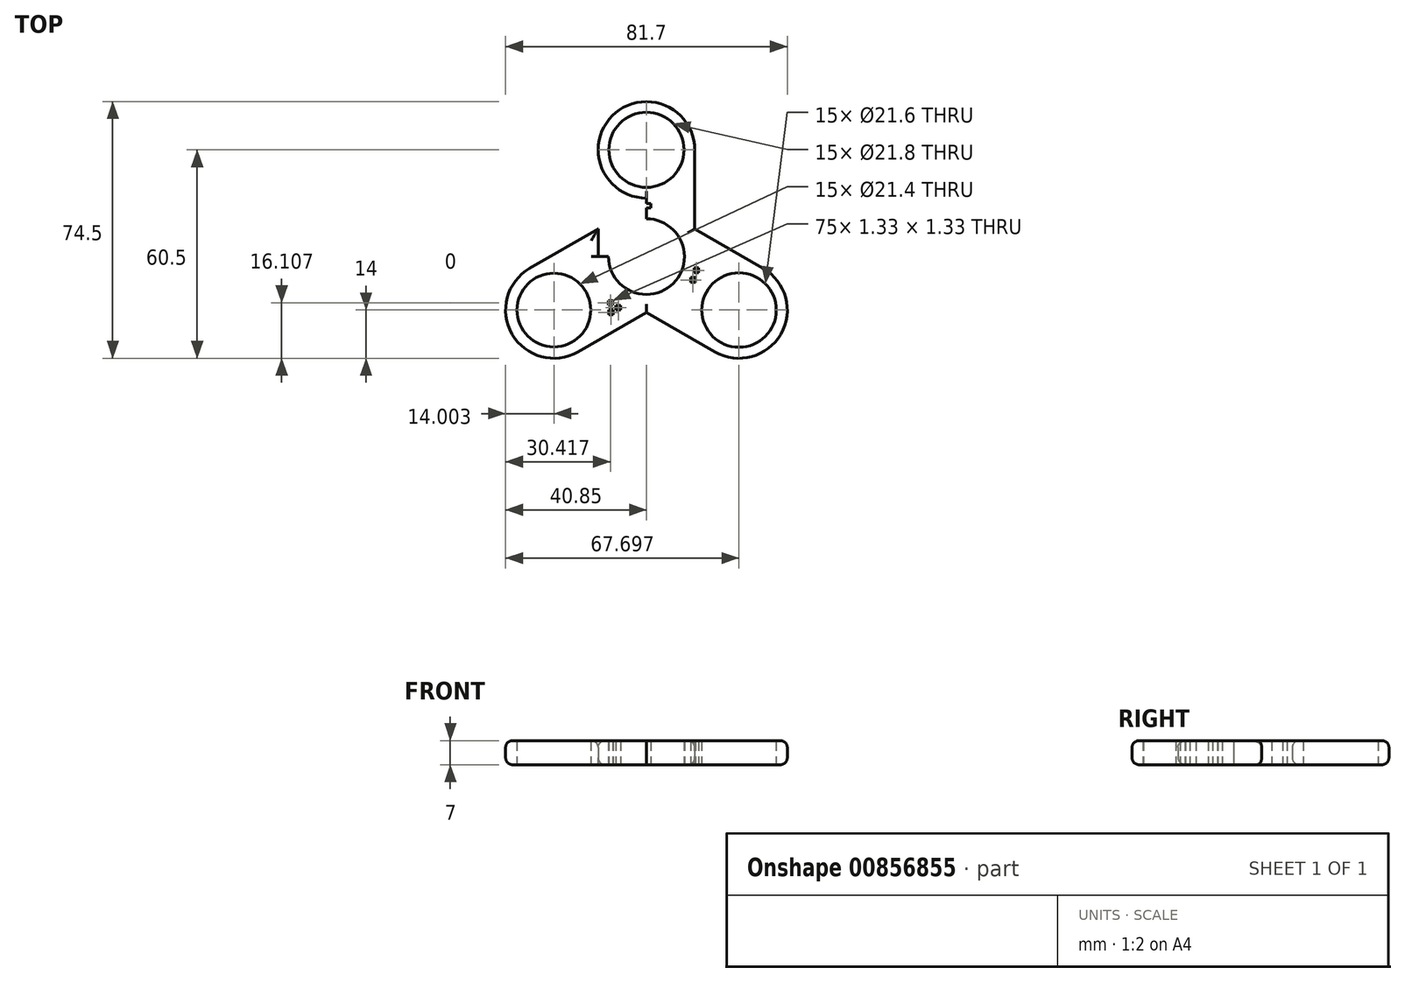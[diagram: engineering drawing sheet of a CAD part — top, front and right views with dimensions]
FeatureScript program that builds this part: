
annotation { "Feature Type Name" : "Feature", "Feature Type Description" : "" }
export const myFeature = defineFeature(function(context is Context, id is Id, definition is map)
    precondition{}
    {
        {
            var Q0;
            Q0=qCreatedBy(makeId("Top.planeOp"),FACE);
            var sketch = newSketch(context, id + "F0", { "sketchPlane" : qUnion([Q0])});
            skLineSegment(sketch, "E0", {"start": v(0, 0) * mm, "end": v(0, 45) * mm});
            skLineSegment(sketch, "E1", {"start": v(0, 45) * mm, "end": v(-14, 45) * mm});
            skLineSegment(sketch, "E2", {"start": v(0, 45) * mm, "end": v(14, 45) * mm});
            skLineSegment(sketch, "E3", {"start": v(-14, 45) * mm, "end": v(-14, 0) * mm});
            skLineSegment(sketch, "E4", {"start": v(-14, 0) * mm, "end": v(0, 0) * mm});
            skLineSegment(sketch, "E5", {"start": v(14, 45) * mm, "end": v(14, 0) * mm});
            skLineSegment(sketch, "E6", {"start": v(14, 0) * mm, "end": v(0, 0) * mm});
            skCircle(sketch, "E7", {"center": v(0, 0) * mm, "radius": 11 * mm});
            skLineSegment(sketch, "E8", {"start": v(0, 45) * mm, "end": v(0, 31) * mm});
            skLineSegment(sketch, "E9", {"start": v(0, 0) * mm, "end": v(38.97, -22.5) * mm});
            skLineSegment(sketch, "E10", {"start": v(0, 0) * mm, "end": v(-38.97, -22.5) * mm});
            skCircle(sketch, "E11", {"center": v(0, 31) * mm, "radius": 14 * mm});
            skLineSegment(sketch, "E12", {"start": v(-38.97, -22.5) * mm, "end": v(-45.97, -10.38) * mm});
            skLineSegment(sketch, "E13", {"start": v(-38.97, -22.5) * mm, "end": v(-31.97, -34.62) * mm});
            skLineSegment(sketch, "E14", {"start": v(38.97, -22.5) * mm, "end": v(31.97, -34.62) * mm});
            skLineSegment(sketch, "E15", {"start": v(38.97, -22.5) * mm, "end": v(45.97, -10.38) * mm});
            skLineSegment(sketch, "E16", {"start": v(45.97, -10.38) * mm, "end": v(14, 8.08) * mm});
            skLineSegment(sketch, "E17", {"start": v(31.97, -34.62) * mm, "end": v(-14, -8.08) * mm});
            skLineSegment(sketch, "E18", {"start": v(-45.97, -10.38) * mm, "end": v(-14, 8.08) * mm});
            skLineSegment(sketch, "E19", {"start": v(-31.97, -34.62) * mm, "end": v(0, -16.17) * mm});
            skLineSegment(sketch, "E20", {"start": v(-38.97, -22.5) * mm, "end": v(-26.85, -15.5) * mm});
            skLineSegment(sketch, "E21", {"start": v(38.97, -22.5) * mm, "end": v(26.85, -15.5) * mm});
            skCircle(sketch, "E22", {"center": v(-26.85, -15.5) * mm, "radius": 14 * mm});
            skCircle(sketch, "E23", {"center": v(26.85, -15.5) * mm, "radius": 14 * mm});
            skCircle(sketch, "E24", {"center": v(-26.85, -15.5) * mm, "radius": 10.7 * mm});
            skCircle(sketch, "E25", {"center": v(26.85, -15.5) * mm, "radius": 10.8 * mm});
            skCircle(sketch, "E26", {"center": v(0, 31) * mm, "radius": 10.9 * mm});
            skLineSegment(sketch, "E27.bottom", {"start": v(0, 14.15) * mm, "end": v(1.33, 14.15) * mm});
            skLineSegment(sketch, "E27.top", {"start": v(0, 15.48) * mm, "end": v(1.33, 15.48) * mm});
            skLineSegment(sketch, "E27.left", {"start": v(0, 14.15) * mm, "end": v(0, 15.48) * mm});
            skLineSegment(sketch, "E27.right", {"start": v(1.33, 14.15) * mm, "end": v(1.33, 15.48) * mm});
            skLineSegment(sketch, "E28.bottom", {"start": v(12.85, -7.42) * mm, "end": v(14.18, -7.42) * mm});
            skLineSegment(sketch, "E28.top", {"start": v(12.85, -6.1) * mm, "end": v(14.18, -6.1) * mm});
            skLineSegment(sketch, "E28.left", {"start": v(12.85, -7.42) * mm, "end": v(12.85, -6.1) * mm});
            skLineSegment(sketch, "E28.right", {"start": v(14.18, -7.42) * mm, "end": v(14.18, -6.1) * mm});
            skLineSegment(sketch, "E29.bottom", {"start": v(13.8, -3.3) * mm, "end": v(15.13, -3.3) * mm});
            skLineSegment(sketch, "E29.top", {"start": v(13.8, -4.62) * mm, "end": v(15.13, -4.62) * mm});
            skLineSegment(sketch, "E29.left", {"start": v(13.8, -3.3) * mm, "end": v(13.8, -4.62) * mm});
            skLineSegment(sketch, "E29.right", {"start": v(15.13, -3.3) * mm, "end": v(15.13, -4.62) * mm});
            skLineSegment(sketch, "E30.bottom", {"start": v(-11.1, -12.73) * mm, "end": v(-9.77, -12.73) * mm});
            skLineSegment(sketch, "E30.top", {"start": v(-11.1, -14.06) * mm, "end": v(-9.77, -14.06) * mm});
            skLineSegment(sketch, "E30.left", {"start": v(-11.1, -12.73) * mm, "end": v(-11.1, -14.06) * mm});
            skLineSegment(sketch, "E30.right", {"start": v(-9.77, -12.73) * mm, "end": v(-9.77, -14.06) * mm});
            skLineSegment(sketch, "E31.bottom", {"start": v(-8.82, -14.17) * mm, "end": v(-7.5, -14.17) * mm});
            skLineSegment(sketch, "E31.top", {"start": v(-8.82, -15.5) * mm, "end": v(-7.5, -15.5) * mm});
            skLineSegment(sketch, "E31.left", {"start": v(-8.82, -14.17) * mm, "end": v(-8.82, -15.5) * mm});
            skLineSegment(sketch, "E31.right", {"start": v(-7.5, -14.17) * mm, "end": v(-7.5, -15.5) * mm});
            skLineSegment(sketch, "E32.bottom", {"start": v(-10.96, -15.5) * mm, "end": v(-9.64, -15.5) * mm});
            skLineSegment(sketch, "E32.top", {"start": v(-10.96, -16.83) * mm, "end": v(-9.64, -16.83) * mm});
            skLineSegment(sketch, "E32.left", {"start": v(-10.96, -15.5) * mm, "end": v(-10.96, -16.83) * mm});
            skLineSegment(sketch, "E32.right", {"start": v(-9.64, -15.5) * mm, "end": v(-9.64, -16.83) * mm});
            skSolve(sketch);
        }
        {
            var Q0;
            {var subQ0=sQuery(id+"F0.wireOp",EDGE,"E11");var subQ4=sQuery(id+"F0.wireOp",EDGE,"E0");var subQ5=makeQuery(id+"F0.imprint","INTERSECT",VERTEX,{"derivedFrom":[subQ4,subQ0]});Q0=makeQuery(id+"F0.imprint","IMPRINT",FACE,{"disambiguationData":[TD([[makeQuery(id+"F0.imprint","IMPRINT",EDGE,{"disambiguationData":[TD([[subQ5,-1.0]])],"derivedFrom":subQ4}),-1.0]])]});}
            var Q1;
            {var subQ0=sQuery(id+"F0.wireOp",EDGE,"E11");var subQ2=sQuery(id+"F0.wireOp",EDGE,"E0");var subQ3=makeQuery(id+"F0.imprint","INTERSECT",VERTEX,{"derivedFrom":[subQ2,subQ0]});Q1=makeQuery(id+"F0.imprint","IMPRINT",FACE,{"disambiguationData":[TD([[makeQuery(id+"F0.imprint","IMPRINT",EDGE,{"disambiguationData":[TD([[subQ3,-1.0]])],"derivedFrom":subQ2}),1.0]])]});}
            var Q2;
            {var subQ6=sQuery(id+"F0.wireOp",EDGE,"E27.left");Q2=makeQuery(id+"F0.imprint","IMPRINT",FACE,{"disambiguationData":[TD([[makeQuery(id+"F0.imprint","IMPRINT",EDGE,{"derivedFrom":subQ6}),1.0]])]});}
            var Q3;
            {var subQ4=sQuery(id+"F0.wireOp",EDGE,"E27.bottom");Q3=makeQuery(id+"F0.imprint","IMPRINT",FACE,{"disambiguationData":[TD([[makeQuery(id+"F0.imprint","IMPRINT",EDGE,{"derivedFrom":subQ4}),-1.0]])]});}
            var Q4;
            {var subQ1=sQuery(id+"F0.wireOp",EDGE,"E28.bottom");Q4=makeQuery(id+"F0.imprint","IMPRINT",FACE,{"disambiguationData":[TD([[makeQuery(id+"F0.imprint","IMPRINT",EDGE,{"derivedFrom":subQ1}),-1.0]])]});}
            var Q5;
            {var subQ5=sQuery(id+"F0.wireOp",EDGE,"E10");var subQ7=sQuery(id+"F0.wireOp",EDGE,"E7");var subQ8=makeQuery(id+"F0.imprint","INTERSECT",VERTEX,{"derivedFrom":[subQ7,subQ5]});Q5=makeQuery(id+"F0.imprint","IMPRINT",FACE,{"disambiguationData":[TD([[makeQuery(id+"F0.imprint","IMPRINT",EDGE,{"disambiguationData":[TD([[subQ8,-1.0]])],"derivedFrom":subQ7}),-1.0]])]});}
            var Q6;
            {var subQ4=sQuery(id+"F0.wireOp",EDGE,"E4");var subQ6=sQuery(id+"F0.wireOp",EDGE,"E3");var subQ7=makeQuery(id+"F0.imprint","INTERSECT",VERTEX,{"derivedFrom":[subQ6,subQ4]});Q6=makeQuery(id+"F0.imprint","IMPRINT",FACE,{"disambiguationData":[TD([[makeQuery(id+"F0.imprint","IMPRINT",EDGE,{"disambiguationData":[TD([[subQ7,1.0]])],"derivedFrom":subQ6}),-1.0]])]});}
            var Q7;
            Q7=makeQuery(id+"F0.imprint","IMPRINT",FACE,{"disambiguationData":[TD([[makeQuery(id+"F0.imprint","IMPRINT",EDGE,{"derivedFrom":sQuery(id+"F0.wireOp",EDGE,"E30.bottom")}),1.0]])]});
            var Q8;
            {var subQ0=sQuery(id+"F0.wireOp",EDGE,"E22");var subQ2=sQuery(id+"F0.wireOp",EDGE,"E10");var subQ3=makeQuery(id+"F0.imprint","INTERSECT",VERTEX,{"derivedFrom":[subQ2,subQ0]});Q8=makeQuery(id+"F0.imprint","IMPRINT",FACE,{"disambiguationData":[TD([[makeQuery(id+"F0.imprint","IMPRINT",EDGE,{"disambiguationData":[TD([[subQ3,-1.0]])],"derivedFrom":subQ2}),1.0]])]});}
            var Q9;
            {var subQ0=sQuery(id+"F0.wireOp",EDGE,"E22");var subQ2=sQuery(id+"F0.wireOp",EDGE,"E10");var subQ3=makeQuery(id+"F0.imprint","INTERSECT",VERTEX,{"derivedFrom":[subQ2,subQ0]});Q9=makeQuery(id+"F0.imprint","IMPRINT",FACE,{"disambiguationData":[TD([[makeQuery(id+"F0.imprint","IMPRINT",EDGE,{"disambiguationData":[TD([[subQ3,-1.0]])],"derivedFrom":subQ2}),-1.0]])]});}
            var Q10;
            {var subQ0=sQuery(id+"F0.wireOp",EDGE,"E23");var subQ2=sQuery(id+"F0.wireOp",EDGE,"E9");var subQ3=makeQuery(id+"F0.imprint","INTERSECT",VERTEX,{"derivedFrom":[subQ2,subQ0]});Q10=makeQuery(id+"F0.imprint","IMPRINT",FACE,{"disambiguationData":[TD([[makeQuery(id+"F0.imprint","IMPRINT",EDGE,{"disambiguationData":[TD([[subQ3,-1.0]])],"derivedFrom":subQ2}),1.0]])]});}
            var Q11;
            {var subQ0=sQuery(id+"F0.wireOp",EDGE,"E23");var subQ4=sQuery(id+"F0.wireOp",EDGE,"E9");var subQ5=makeQuery(id+"F0.imprint","INTERSECT",VERTEX,{"derivedFrom":[subQ4,subQ0]});Q11=makeQuery(id+"F0.imprint","IMPRINT",FACE,{"disambiguationData":[TD([[makeQuery(id+"F0.imprint","IMPRINT",EDGE,{"disambiguationData":[TD([[subQ5,-1.0]])],"derivedFrom":subQ4}),-1.0]])]});}
            extrude(context, id + "F1", {"entities" : qUnion([Q0, Q1, Q2, Q3, Q4, Q5, Q6, Q7, Q8, Q9, Q10, Q11]), "depth" : 7 * mm, "offsetDistance" : 25 * mm});
        }
        {
            var Q0;
            Q0=makeQuery(id+"F1.opExtrude","CAP_EDGE",EDGE,{"disambiguationData":[OSD([sQuery(id+"F0.wireOp",EDGE,"E3")])],"isStart":false});
            var Q1;
            Q1=makeQuery(id+"F1.opExtrude","CAP_EDGE",EDGE,{"disambiguationData":[OSD([sQuery(id+"F0.wireOp",EDGE,"E11")])],"isStart":false});
            var Q2;
            Q2=makeQuery(id+"F1.opExtrude","CAP_EDGE",EDGE,{"disambiguationData":[OSD([sQuery(id+"F0.wireOp",EDGE,"E18")])],"isStart":false});
            var Q3;
            Q3=makeQuery(id+"F1.opExtrude","CAP_EDGE",EDGE,{"disambiguationData":[OSD([sQuery(id+"F0.wireOp",EDGE,"E22")])],"isStart":false});
            var Q4;
            Q4=makeQuery(id+"F1.opExtrude","CAP_EDGE",EDGE,{"disambiguationData":[OSD([sQuery(id+"F0.wireOp",EDGE,"E19")])],"isStart":false});
            var Q5;
            Q5=makeQuery(id+"F1.opExtrude","CAP_EDGE",EDGE,{"disambiguationData":[OSD([sQuery(id+"F0.wireOp",EDGE,"E17")])],"isStart":false});
            var Q6;
            Q6=makeQuery(id+"F1.opExtrude","CAP_EDGE",EDGE,{"disambiguationData":[OSD([sQuery(id+"F0.wireOp",EDGE,"E23")])],"isStart":false});
            var Q7;
            Q7=makeQuery(id+"F1.opExtrude","CAP_EDGE",EDGE,{"disambiguationData":[OSD([sQuery(id+"F0.wireOp",EDGE,"E16")])],"isStart":false});
            var Q8;
            Q8=makeQuery(id+"F1.opExtrude","CAP_EDGE",EDGE,{"disambiguationData":[OSD([sQuery(id+"F0.wireOp",EDGE,"E5")])],"isStart":false});
            var Q9;
            Q9=makeQuery(id+"F1.opExtrude","CAP_EDGE",EDGE,{"disambiguationData":[OSD([sQuery(id+"F0.wireOp",EDGE,"E19")])],"isStart":true});
            var Q10;
            Q10=makeQuery(id+"F1.opExtrude","CAP_EDGE",EDGE,{"disambiguationData":[OSD([sQuery(id+"F0.wireOp",EDGE,"E22")])],"isStart":true});
            var Q11;
            Q11=makeQuery(id+"F1.opExtrude","CAP_EDGE",EDGE,{"disambiguationData":[OSD([sQuery(id+"F0.wireOp",EDGE,"E17")])],"isStart":true});
            var Q12;
            Q12=makeQuery(id+"F1.opExtrude","CAP_EDGE",EDGE,{"disambiguationData":[OSD([sQuery(id+"F0.wireOp",EDGE,"E23")])],"isStart":true});
            var Q13;
            Q13=makeQuery(id+"F1.opExtrude","CAP_EDGE",EDGE,{"disambiguationData":[OSD([sQuery(id+"F0.wireOp",EDGE,"E16")])],"isStart":true});
            var Q14;
            Q14=makeQuery(id+"F1.opExtrude","CAP_EDGE",EDGE,{"disambiguationData":[OSD([sQuery(id+"F0.wireOp",EDGE,"E5")])],"isStart":true});
            var Q15;
            Q15=makeQuery(id+"F1.opExtrude","CAP_EDGE",EDGE,{"disambiguationData":[OSD([sQuery(id+"F0.wireOp",EDGE,"E11")])],"isStart":true});
            fillet(context, id + "F2", {"entities" : qUnion([Q0, Q1, Q2, Q3, Q4, Q5, Q6, Q7, Q8, Q9, Q10, Q11, Q12, Q13, Q14, Q15]), "radius" : 2 * mm, "tangentPropagation" : true, "allowEdgeOverflow" : false});
        }
    });
